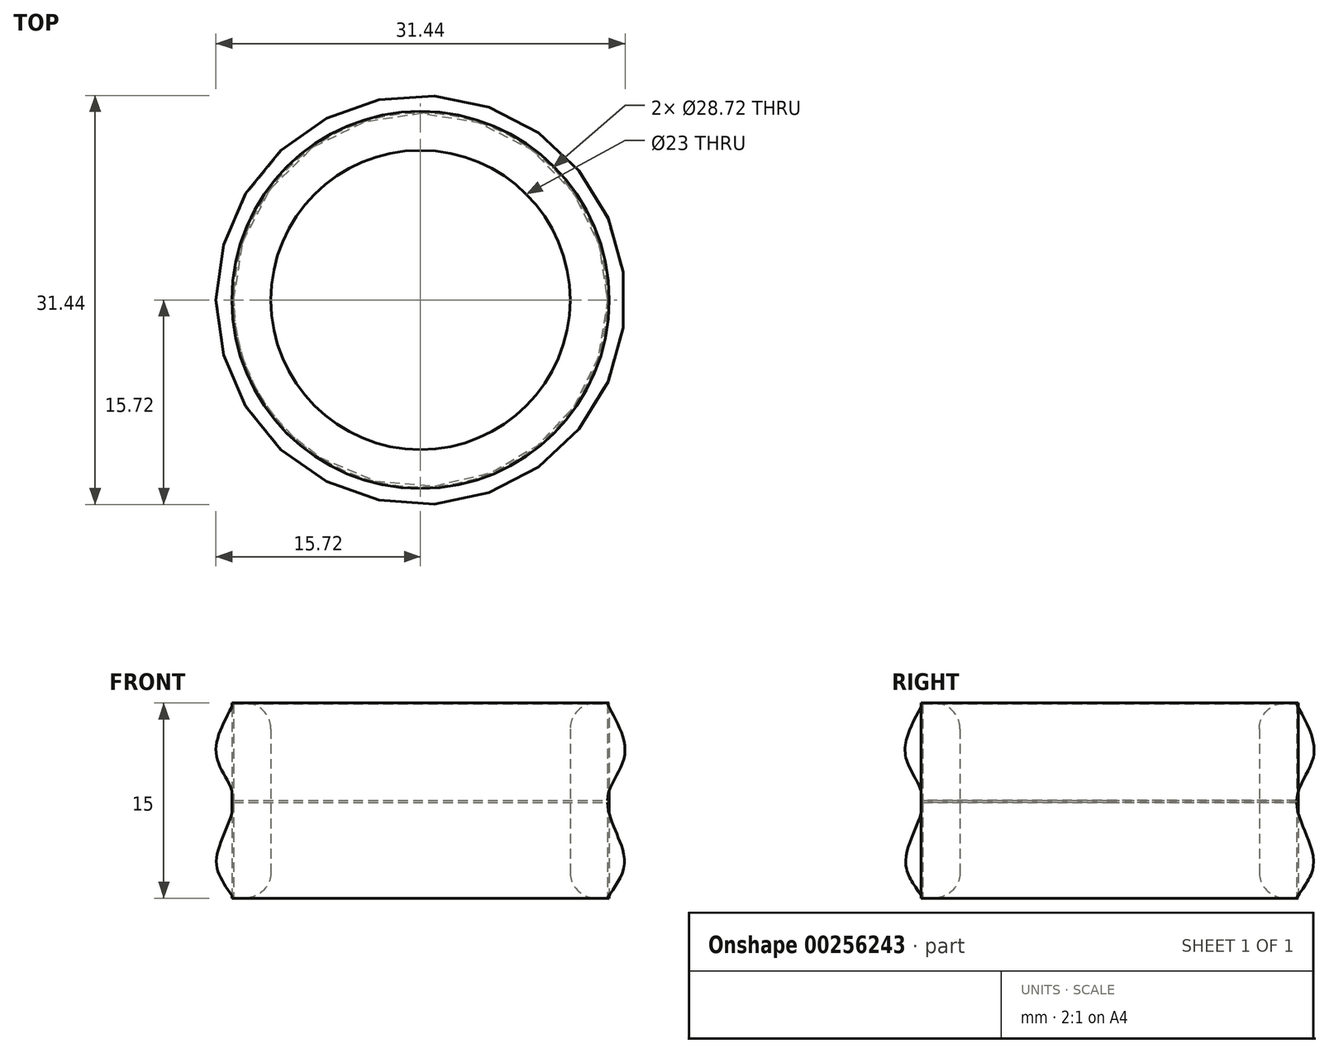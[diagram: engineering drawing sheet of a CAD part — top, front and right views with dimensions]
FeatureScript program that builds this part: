
annotation { "Feature Type Name" : "Feature", "Feature Type Description" : "" }
export const myFeature = defineFeature(function(context is Context, id is Id, definition is map)
    precondition{}
    {
        {
            var Q0;
            Q0=qCreatedBy(makeId("Top.planeOp"),FACE);
            var sketch = newSketch(context, id + "F0", { "sketchPlane" : qUnion([Q0])});
            skCircle(sketch, "E0", {"center": v(0, 0) * mm, "radius": 11.5 * mm});
            skCircle(sketch, "E1", {"center": v(0, 0) * mm, "radius": 14.5 * mm});
            skSolve(sketch);
        }
        {
            var Q0;
            Q0 = qSketchRegion(id + "F0", true);
            extrude(context, id + "F1", {"entities" : qUnion([Q0]), "depth" : 15 * mm});
        }
        {
            var Q0;
            Q0=qCreatedBy(makeId("Right.planeOp"),FACE);
            var sketch = newSketch(context, id + "F2", { "sketchPlane" : qUnion([Q0])});
            skPoint(sketch, "E2", {"position": v(14.36, 0) * mm});
            skPoint(sketch, "E3", {"position": v(14.36, 14.93) * mm});
            skFitSpline(sketch, "E4", {"points": [v(14.36, 0) * mm, v(15.68, 2.93) * mm, v(14.36, 7.5) * mm, v(15.68, 10.93) * mm, v(14.36, 14.93) * mm], "startDerivative": vector(7.83, 12.37) * mm, "endDerivative": vector(-8.82, 16.19) * mm});
            skLineSegment(sketch, "E5", {"start": v(14.36, 0) * mm, "end": v(14.36, 14.93) * mm});
            skSolve(sketch);
        }
        {
            var Q0;
            Q0 = qSketchRegion(id + "F2", true);
            var Q1;
            Q1=makeQuery(id+"F1.opExtrude","CAP_EDGE",EDGE,{"disambiguationData":[OSD([sQuery(id+"F0.wireOp",EDGE,"E0")])],"isStart":true});
            revolve(context, id + "F3", {"entities" : qUnion([Q0]), "axis" : qUnion([Q1]), "revolveType" : RevolveType.FULL});
        }
        {
            var Q0;
            Q0=makeQuery(id+"F1.opExtrude","CAP_EDGE",EDGE,{"disambiguationData":[OSD([sQuery(id+"F0.wireOp",EDGE,"E0")])],"isStart":true});
            var Q1;
            Q1=makeQuery(id+"F1.opExtrude","CAP_EDGE",EDGE,{"disambiguationData":[OSD([sQuery(id+"F0.wireOp",EDGE,"E0")])],"isStart":false});
            fillet(context, id + "F4", {"entities" : qUnion([Q0, Q1]), "radius" : 2 * mm, "tangentPropagation" : true, "allowEdgeOverflow" : false});
        }
    });
